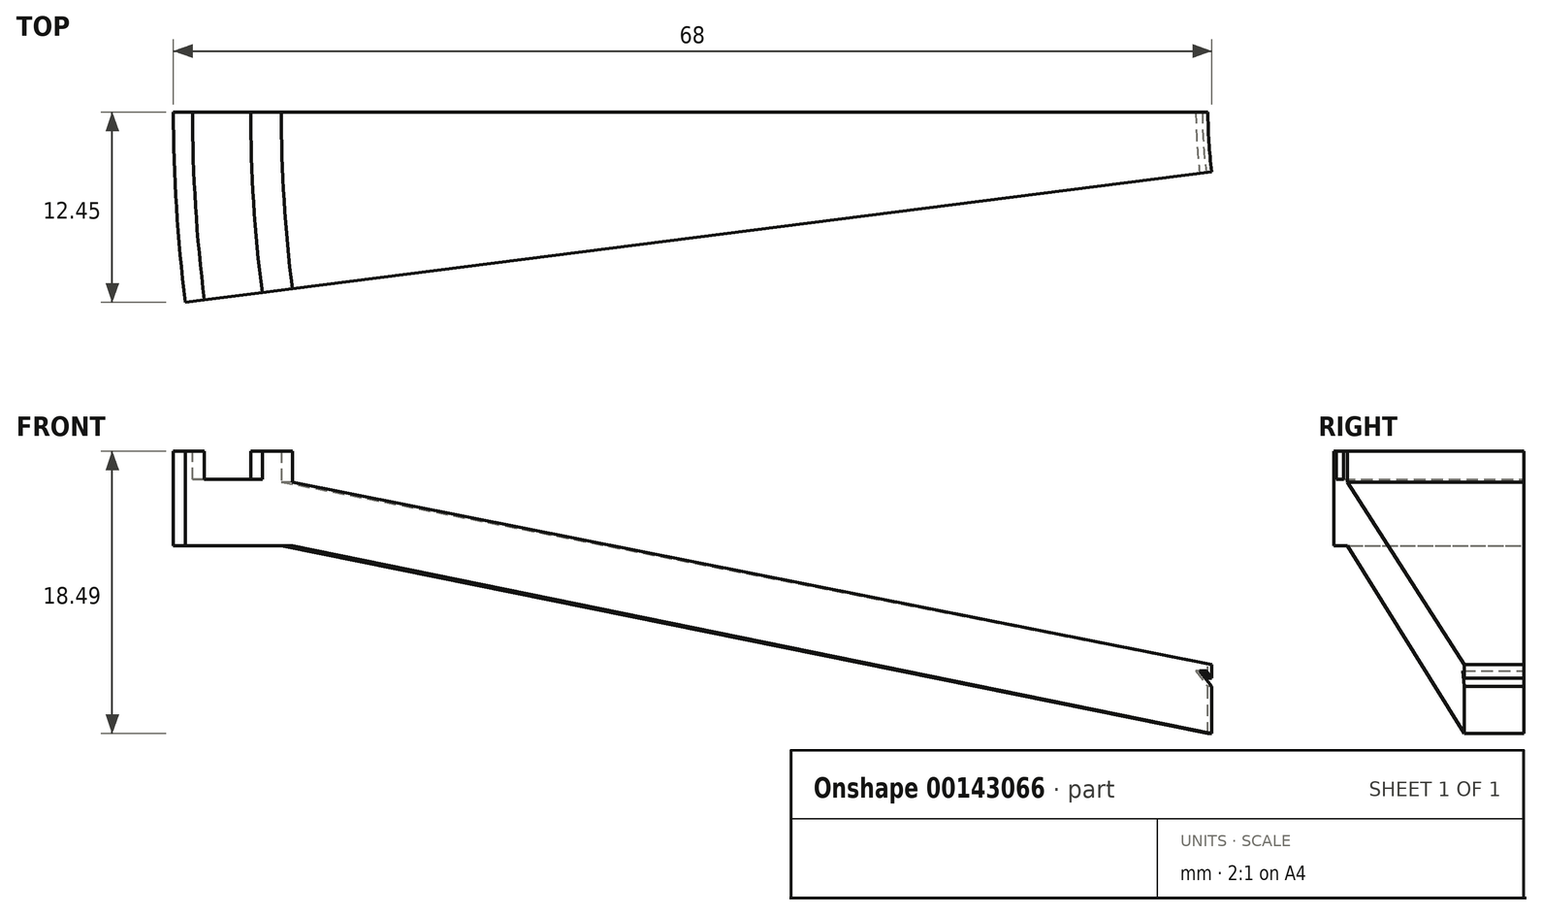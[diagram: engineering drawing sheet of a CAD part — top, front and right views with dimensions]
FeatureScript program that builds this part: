
annotation { "Feature Type Name" : "Feature", "Feature Type Description" : "" }
export const myFeature = defineFeature(function(context is Context, id is Id, definition is map)
    precondition{}
    {
        {
            var Q0;
            Q0=qCreatedBy(makeId("Front.planeOp"),FACE);
            var sketch = newSketch(context, id + "F0", { "sketchPlane" : qUnion([Q0])});
            skLineSegment(sketch, "E0", {"start": v(-14.4, 11.61) * mm, "end": v(-14.4, 59.6) * mm});
            skLineSegment(sketch, "E1", {"start": v(-111.77, 68.8) * mm, "end": v(-107.96, 68.8) * mm});
            skLineSegment(sketch, "E2", {"start": v(-107.96, 68.8) * mm, "end": v(-107.96, 70.64) * mm});
            skLineSegment(sketch, "E3", {"start": v(-107.96, 70.64) * mm, "end": v(-105.97, 70.64) * mm});
            skLineSegment(sketch, "E4", {"start": v(-105.97, 70.64) * mm, "end": v(-105.97, 68.62) * mm});
            skLineSegment(sketch, "E5", {"start": v(-111.77, 68.8) * mm, "end": v(-111.77, 70.64) * mm});
            skLineSegment(sketch, "E6", {"start": v(-105.97, 68.62) * mm, "end": v(-45.28, 56.68) * mm});
            skLineSegment(sketch, "E7", {"start": v(-113.03, 67.22) * mm, "end": v(-113.03, 70.64) * mm});
            skLineSegment(sketch, "E8", {"start": v(-113.03, 70.64) * mm, "end": v(-111.77, 70.64) * mm});
            skLineSegment(sketch, "E9", {"start": v(-45.28, 55.8) * mm, "end": v(-45.64, 56.25) * mm});
            skLineSegment(sketch, "E10", {"start": v(-45.64, 56.25) * mm, "end": v(-46.07, 56.25) * mm});
            skLineSegment(sketch, "E11", {"start": v(-46.07, 56.25) * mm, "end": v(-45.28, 55.22) * mm});
            skLineSegment(sketch, "E12", {"start": v(-45.28, 54.9) * mm, "end": v(-45.28, 55.22) * mm});
            skLineSegment(sketch, "E13", {"start": v(-45.28, 55.8) * mm, "end": v(-45.28, 56.68) * mm});
            skLineSegment(sketch, "E14", {"start": v(-113.03, 67.22) * mm, "end": v(-113.03, 64.46) * mm});
            skLineSegment(sketch, "E15", {"start": v(-113.03, 64.46) * mm, "end": v(-105.97, 64.46) * mm});
            skLineSegment(sketch, "E16", {"start": v(-105.97, 64.46) * mm, "end": v(-45.28, 52.15) * mm});
            skLineSegment(sketch, "E17", {"start": v(-45.28, 52.15) * mm, "end": v(-45.28, 54.9) * mm});
            skSolve(sketch);
        }
        {
            var Q0;
            Q0=makeQuery(id+"F0.imprint","IMPRINT",FACE,{"disambiguationData":[TD([[makeQuery(id+"F0.imprint","IMPRINT",EDGE,{"derivedFrom":sQuery(id+"F0.wireOp",EDGE,"E1")}),-1.0]])]});
            var Q1;
            Q1=sQuery(id+"F0.wireOp",EDGE,"E0");
            revolve(context, id + "F1", {"entities" : qUnion([Q0]), "axis" : qUnion([Q1]), "revolveType" : RevolveType.ONE_DIRECTION, "angle" : 7.25 * degree});
        }
    });
